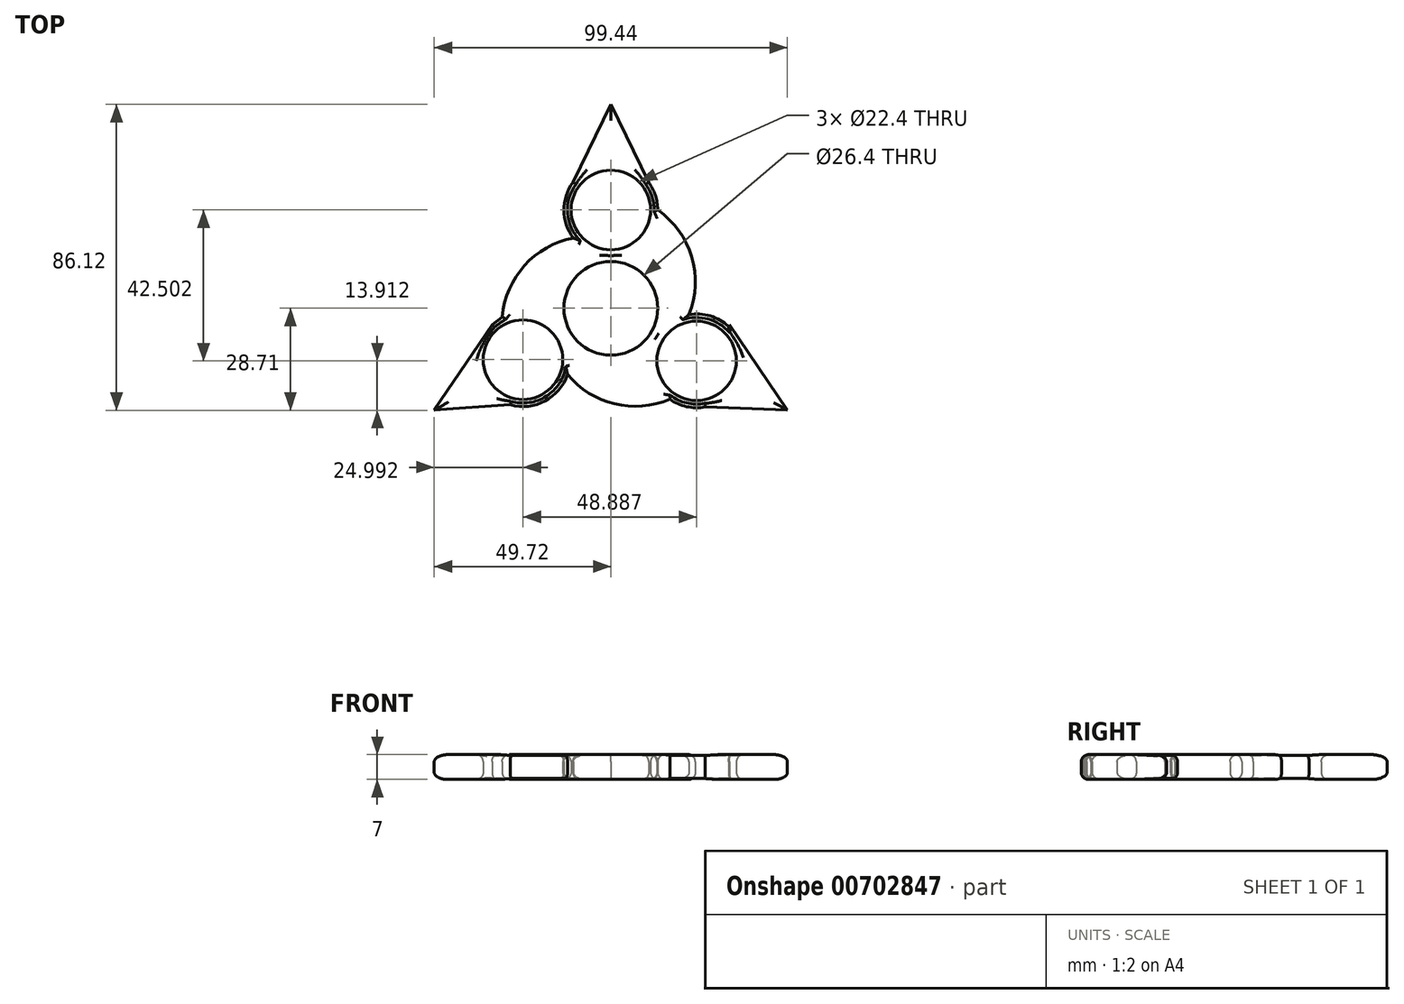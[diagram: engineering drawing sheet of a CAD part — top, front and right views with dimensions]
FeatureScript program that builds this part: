
annotation { "Feature Type Name" : "Feature", "Feature Type Description" : "" }
export const myFeature = defineFeature(function(context is Context, id is Id, definition is map)
    precondition{}
    {
        {
            var Q0;
            Q0=qCreatedBy(makeId("Top.planeOp"),FACE);
            var sketch = newSketch(context, id + "F0", { "sketchPlane" : qUnion([Q0])});
            skCircle(sketch, "E0", {"center": v(0, 0) * mm, "radius": 11.2 * mm});
            skCircle(sketch, "E1", {"center": v(0, 0) * mm, "radius": 13.2 * mm});
            skCircle(sketch, "E2", {"center": v(0, 27.7) * mm, "radius": 11.2 * mm});
            skArc(sketch, "E3", {"start": v(13.2, 27.7) * mm, "mid": v(-4.18, 40.22) * mm, "end": v(-10.55, 19.77) * mm});
            skPoint(sketch, "E4.center", {"position": v(-0.08, -0.01) * mm});
            skCircle(sketch, "E5.1.0", {"center": v(-24.73, -14.47) * mm, "radius": 11.2 * mm});
            skArc(sketch, "E5.1.1", {"start": v(-37.23, -10.24) * mm, "mid": v(-28.92, -26.99) * mm, "end": v(-12.2, -18.61) * mm});
            skCircle(sketch, "E5.2.0", {"center": v(24.16, -14.8) * mm, "radius": 11.2 * mm});
            skArc(sketch, "E5.2.1", {"start": v(16.62, -25.63) * mm, "mid": v(37.03, -17.71) * mm, "end": v(22.01, -1.77) * mm});
            skPoint(sketch, "E5.center", {"position": v(-0.19, -0.52) * mm});
            skArc(sketch, "E6", {"start": v(22.01, -1.77) * mm, "mid": v(22.75, 14.5) * mm, "end": v(13.2, 27.7) * mm});
            skLineSegment(sketch, "E7", {"start": v(12.7, 31.29) * mm, "end": v(0, 57.41) * mm});
            skLineSegment(sketch, "E8", {"start": v(0, 57.41) * mm, "end": v(-12.7, 31.29) * mm});
            skLineSegment(sketch, "E9.1.0", {"start": v(-33.45, -4.64) * mm, "end": v(-49.72, -28.7) * mm});
            skLineSegment(sketch, "E9.1.1", {"start": v(-49.72, -28.7) * mm, "end": v(-20.74, -26.65) * mm});
            skLineSegment(sketch, "E9.2.1", {"start": v(49.72, -28.7) * mm, "end": v(33.45, -4.64) * mm});
            skArc(sketch, "E10.1.0", {"start": v(-9.47, 19.95) * mm, "mid": v(-23.94, 12.45) * mm, "end": v(-30.6, -2.42) * mm});
            skArc(sketch, "E10.2.0", {"start": v(-12.54, -18.18) * mm, "mid": v(1.18, -26.95) * mm, "end": v(17.4, -25.28) * mm});
            skLineSegment(sketch, "E11", {"start": v(-33.45, -4.64) * mm, "end": v(-30.6, -2.42) * mm});
            skLineSegment(sketch, "E12", {"start": v(49.72, -28.7) * mm, "end": v(20.74, -27.55) * mm});
            skLineSegment(sketch, "E13", {"start": v(33.45, -4.64) * mm, "end": v(20.74, -27.55) * mm});
            skSolve(sketch);
        }
        {
            var Q0;
            Q0 = qSketchRegion(id + "F0", true);
            extrude(context, id + "F1", {"entities" : qUnion([Q0]), "depth" : 7 * mm, "offsetDistance" : 25 * mm});
        }
        {
            var Q0;
            Q0=makeQuery(id+"F1.opExtrude","CAP_FACE",FACE,{"disambiguationData":[OSD([sQuery(id+"F0.wireOp",EDGE,"E1"),sQuery(id+"F0.wireOp",EDGE,"E2"),sQuery(id+"F0.wireOp",EDGE,"E3"),sQuery(id+"F0.wireOp",EDGE,"E5.1.0"),sQuery(id+"F0.wireOp",EDGE,"E5.1.1"),sQuery(id+"F0.wireOp",EDGE,"E5.2.0"),sQuery(id+"F0.wireOp",EDGE,"E5.2.1"),sQuery(id+"F0.wireOp",EDGE,"E6"),sQuery(id+"F0.wireOp",EDGE,"E7"),sQuery(id+"F0.wireOp",EDGE,"E8"),sQuery(id+"F0.wireOp",EDGE,"E9.1.0"),sQuery(id+"F0.wireOp",EDGE,"E9.1.1"),sQuery(id+"F0.wireOp",EDGE,"E9.2.1"),sQuery(id+"F0.wireOp",EDGE,"E10.1.0"),sQuery(id+"F0.wireOp",EDGE,"E10.2.0"),sQuery(id+"F0.wireOp",EDGE,"E11"),sQuery(id+"F0.wireOp",EDGE,"E12"),sQuery(id+"F0.wireOp",EDGE,"E13")])],"isStart":false});
            var Q1;
            Q1=makeQuery(id+"F1.opExtrude","CAP_FACE",FACE,{"disambiguationData":[OSD([sQuery(id+"F0.wireOp",EDGE,"E1"),sQuery(id+"F0.wireOp",EDGE,"E2"),sQuery(id+"F0.wireOp",EDGE,"E3"),sQuery(id+"F0.wireOp",EDGE,"E5.1.0"),sQuery(id+"F0.wireOp",EDGE,"E5.1.1"),sQuery(id+"F0.wireOp",EDGE,"E5.2.0"),sQuery(id+"F0.wireOp",EDGE,"E5.2.1"),sQuery(id+"F0.wireOp",EDGE,"E6"),sQuery(id+"F0.wireOp",EDGE,"E7"),sQuery(id+"F0.wireOp",EDGE,"E8"),sQuery(id+"F0.wireOp",EDGE,"E9.1.0"),sQuery(id+"F0.wireOp",EDGE,"E9.1.1"),sQuery(id+"F0.wireOp",EDGE,"E9.2.1"),sQuery(id+"F0.wireOp",EDGE,"E10.1.0"),sQuery(id+"F0.wireOp",EDGE,"E10.2.0"),sQuery(id+"F0.wireOp",EDGE,"E11"),sQuery(id+"F0.wireOp",EDGE,"E12"),sQuery(id+"F0.wireOp",EDGE,"E13")])],"isStart":true});
            fillet(context, id + "F2", {"entities" : qUnion([Q0, Q1]), "radius" : 2 * mm, "tangentPropagation" : true, "defaultsChanged" : false, "vertexSettings" : [], "allowEdgeOverflow" : false});
        }
    });
